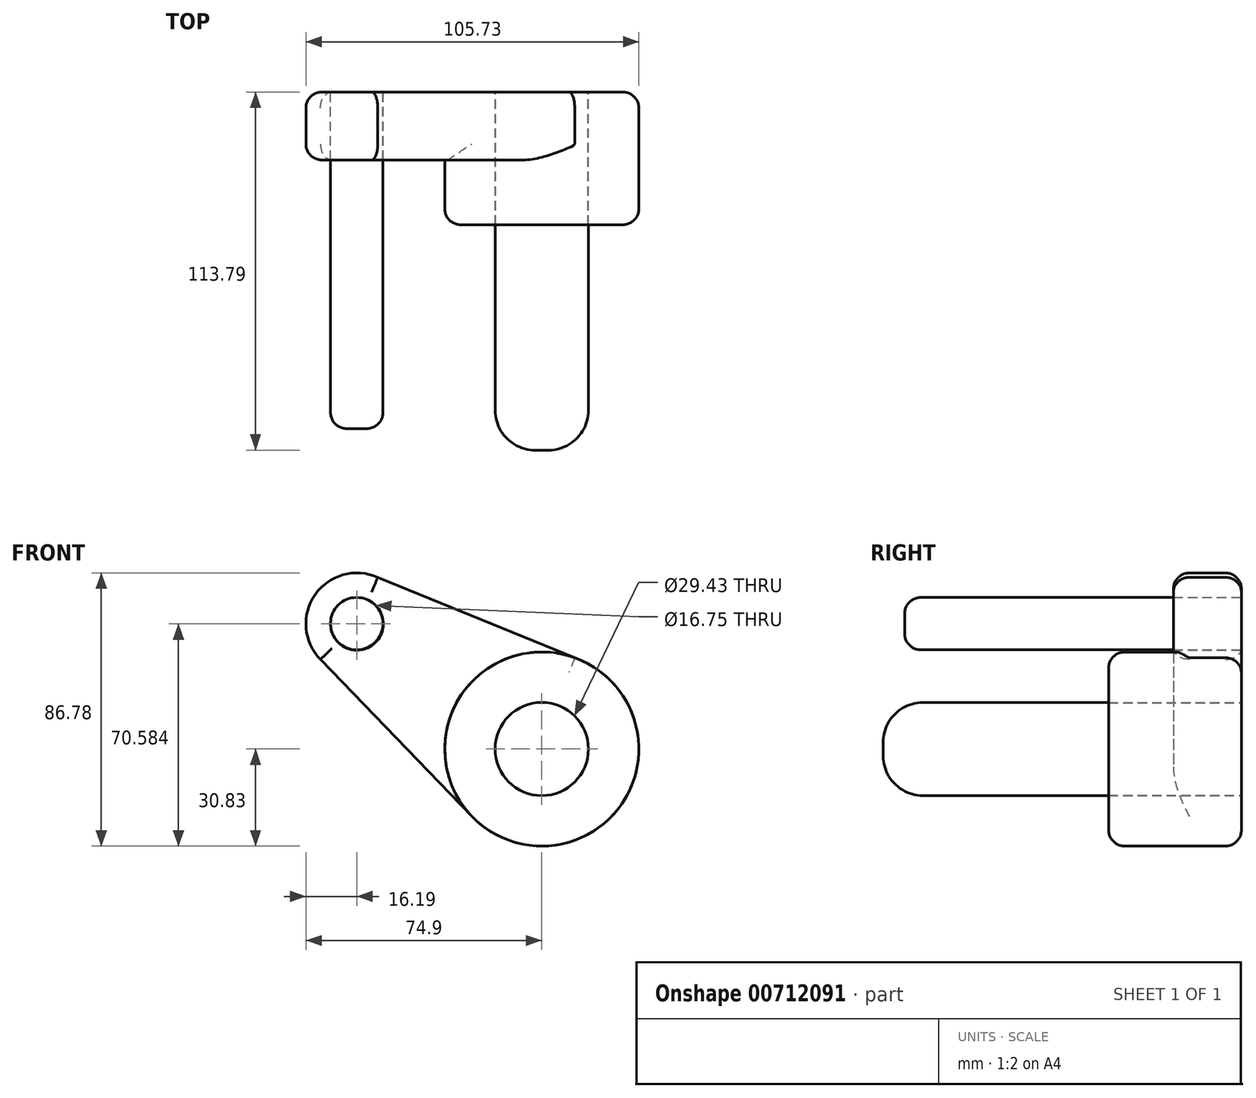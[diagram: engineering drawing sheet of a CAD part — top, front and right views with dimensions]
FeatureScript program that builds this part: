
annotation { "Feature Type Name" : "Feature", "Feature Type Description" : "" }
export const myFeature = defineFeature(function(context is Context, id is Id, definition is map)
    precondition{}
    {
        {
            var Q0;
            Q0=qCreatedBy(makeId("Front.planeOp"),FACE);
            var sketch = newSketch(context, id + "F0", { "sketchPlane" : qUnion([Q0])});
            skCircle(sketch, "E0", {"center": v(0, 0) * mm, "radius": 30.83 * mm});
            skCircle(sketch, "E1", {"center": v(-58.71, 39.75) * mm, "radius": 16.2 * mm});
            skLineSegment(sketch, "E2", {"start": v(-70.3, 28.44) * mm, "end": v(-22.18, -21.4) * mm});
            skLineSegment(sketch, "E3", {"start": v(-52.08, 54.53) * mm, "end": v(10.46, 29) * mm});
            skCircle(sketch, "E4", {"center": v(-58.71, 39.75) * mm, "radius": 8.38 * mm});
            skCircle(sketch, "E5", {"center": v(0, 0) * mm, "radius": 14.71 * mm});
            skSolve(sketch);
        }
        {
            var Q0;
            Q0 = qSketchRegion(id + "F0", true);
            extrude(context, id + "F1", {"entities" : qUnion([Q0]), "depth" : 21.59 * mm, "offsetDistance" : 25.4 * mm});
        }
        {
            var Q0;
            Q0=makeQuery(id+"F0.imprint","IMPRINT",FACE,{"disambiguationData":[TD([[makeQuery(id+"F0.imprint","IMPRINT",EDGE,{"derivedFrom":sQuery(id+"F0.wireOp",EDGE,"E5")}),-1.0]])]});
            extrude(context, id + "F2", {"entities" : qUnion([Q0]), "operationType" : NewBodyOperationType.ADD, "depth" : 42.16 * mm, "offsetDistance" : 25.4 * mm});
        }
        {
            var Q0;
            Q0=makeQuery(id+"F1.opExtrude","CAP_EDGE",EDGE,{"disambiguationData":[OSD([sQuery(id+"F0.wireOp",EDGE,"E3")])],"isStart":false});
            var Q1;
            Q1=makeQuery(id+"F1.opExtrude","CAP_EDGE",EDGE,{"disambiguationData":[OSD([sQuery(id+"F0.wireOp",EDGE,"E2")])],"isStart":false});
            var Q2;
            Q2=makeQuery(id+"F1.opExtrude","CAP_EDGE",EDGE,{"disambiguationData":[OSD([sQuery(id+"F0.wireOp",EDGE,"E1")])],"isStart":false});
            var Q3;
            Q3=makeQuery(id+"F2.opExtrude","CAP_EDGE",EDGE,{"disambiguationData":[OSD([sQuery(id+"F0.wireOp",EDGE,"E0")])],"isStart":false});
            var Q4;
            Q4=makeQuery(id+"F1.opExtrude","CAP_EDGE",EDGE,{"disambiguationData":[OSD([sQuery(id+"F0.wireOp",EDGE,"E3")])],"isStart":true});
            var Q5;
            Q5=makeQuery(id+"F1.opExtrude","CAP_EDGE",EDGE,{"disambiguationData":[OSD([sQuery(id+"F0.wireOp",EDGE,"E1")])],"isStart":true});
            var Q6;
            Q6=makeQuery(id+"F1.opExtrude","CAP_EDGE",EDGE,{"disambiguationData":[OSD([sQuery(id+"F0.wireOp",EDGE,"E0")])],"isStart":true});
            fillet(context, id + "F3", {"entities" : qUnion([Q0, Q1, Q2, Q3, Q4, Q5, Q6]), "radius" : 5.08 * mm, "tangentPropagation" : true, "allowEdgeOverflow" : false});
        }
        {
            var Q0;
            Q0=qCreatedBy(makeId("Front.planeOp"),FACE);
            var sketch = newSketch(context, id + "F4", { "sketchPlane" : qUnion([Q0])});
            skCircle(sketch, "E6", {"center": v(0, 0) * mm, "radius": 14.8 * mm});
            skSolve(sketch);
        }
        {
            var Q0;
            Q0 = qSketchRegion(id + "F4", true);
            extrude(context, id + "F5", {"entities" : qUnion([Q0]), "depth" : 113.8 * mm, "offsetDistance" : 25.4 * mm});
        }
        {
            var Q0;
            Q0=qCreatedBy(makeId("Front.planeOp"),FACE);
            var sketch = newSketch(context, id + "F6", { "sketchPlane" : qUnion([Q0])});
            skCircle(sketch, "E7", {"center": v(-58.76, 39.84) * mm, "radius": 8.32 * mm});
            skSolve(sketch);
        }
        {
            var Q0;
            Q0 = qSketchRegion(id + "F6", true);
            extrude(context, id + "F7", {"entities" : qUnion([Q0]), "depth" : 106.93 * mm, "offsetDistance" : 25.4 * mm});
        }
        {
            var Q0;
            Q0=makeQuery(id+"F5.opExtrude","CAP_FACE",FACE,{"disambiguationData":[OSD([sQuery(id+"F4.wireOp",EDGE,"E6")])],"isStart":false});
            fillet(context, id + "F8", {"entities" : qUnion([Q0]), "radius" : 12.7 * mm, "tangentPropagation" : true, "allowEdgeOverflow" : false});
        }
        {
            var Q0;
            Q0=makeQuery(id+"F7.opExtrude","CAP_FACE",FACE,{"disambiguationData":[OSD([sQuery(id+"F6.wireOp",EDGE,"E7")])],"isStart":false});
            fillet(context, id + "F9", {"entities" : qUnion([Q0]), "radius" : 5.08 * mm, "tangentPropagation" : true, "allowEdgeOverflow" : false});
        }
    });
